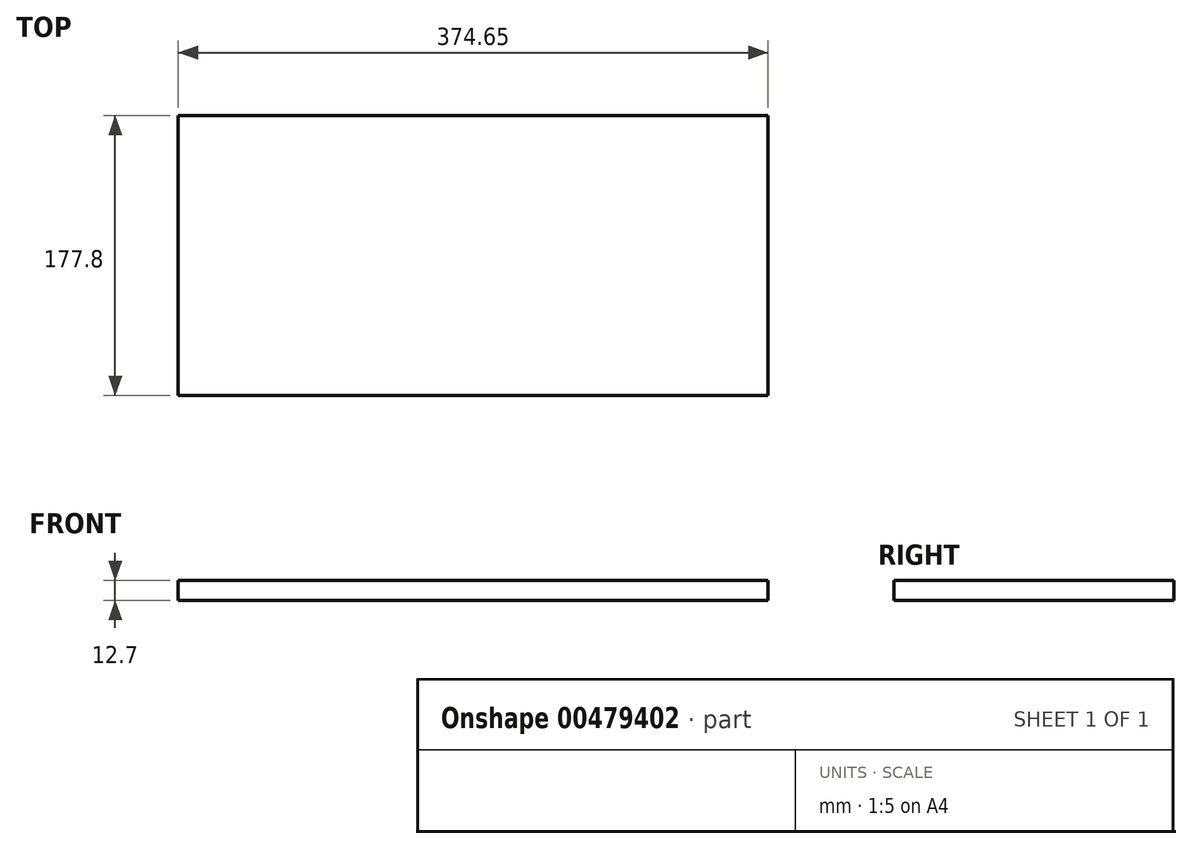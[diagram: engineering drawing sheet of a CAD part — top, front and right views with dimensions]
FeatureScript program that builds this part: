
annotation { "Feature Type Name" : "Feature", "Feature Type Description" : "" }
export const myFeature = defineFeature(function(context is Context, id is Id, definition is map)
    precondition{}
    {
        {
            var Q0;
            Q0=qCreatedBy(makeId("Top.planeOp"),FACE);
            var sketch = newSketch(context, id + "F0", { "sketchPlane" : qUnion([Q0])});
            skLineSegment(sketch, "E0.bottom", {"start": v(0, 0) * mm, "end": v(374.65, 0) * mm});
            skLineSegment(sketch, "E0.top", {"start": v(0, 177.8) * mm, "end": v(374.65, 177.8) * mm});
            skLineSegment(sketch, "E0.left", {"start": v(0, 0) * mm, "end": v(0, 177.8) * mm});
            skLineSegment(sketch, "E0.right", {"start": v(374.65, 0) * mm, "end": v(374.65, 177.8) * mm});
            skSolve(sketch);
        }
        {
            var Q0;
            Q0 = qSketchRegion(id + "F0", true);
            extrude(context, id + "F1", {"entities" : qUnion([Q0]), "depth" : 12.7 * mm, "offsetDistance" : 25.4 * mm});
        }
    });
